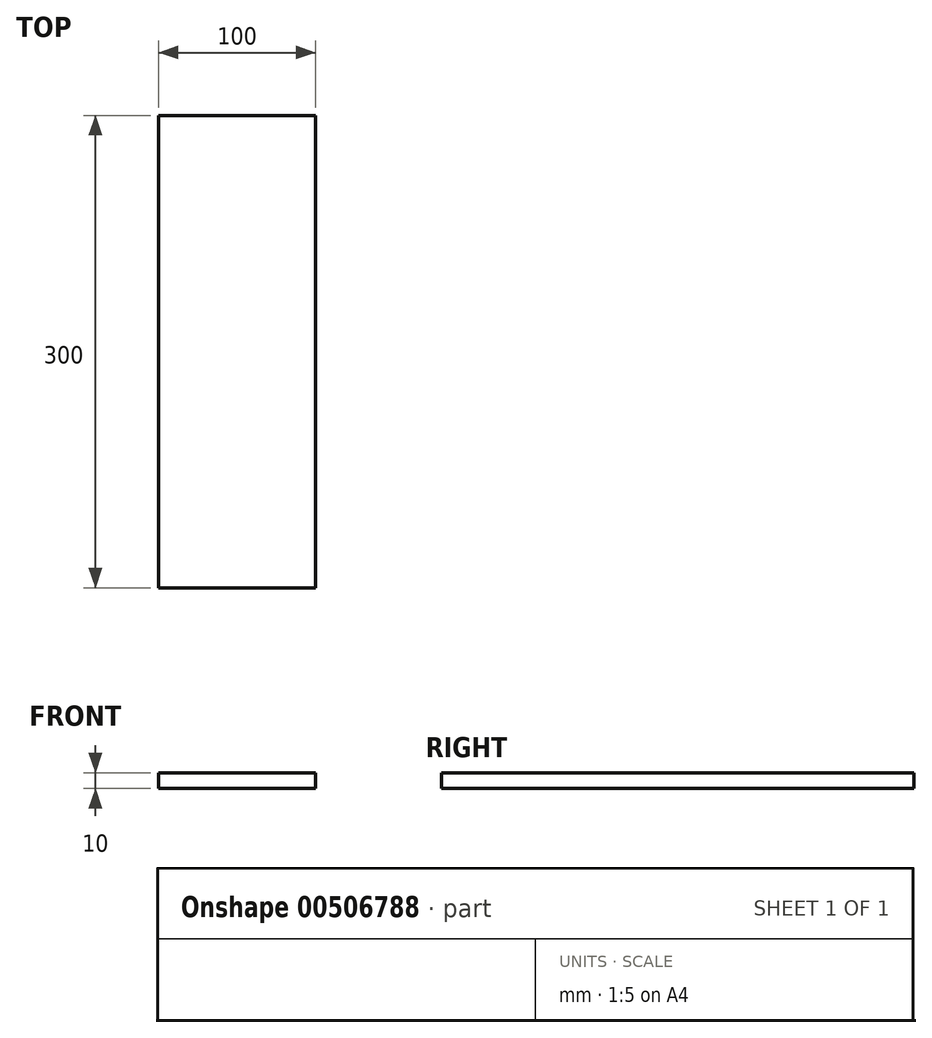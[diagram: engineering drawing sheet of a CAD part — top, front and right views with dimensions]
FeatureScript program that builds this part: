
annotation { "Feature Type Name" : "Feature", "Feature Type Description" : "" }
export const myFeature = defineFeature(function(context is Context, id is Id, definition is map)
    precondition{}
    {
        {
            var Q0;
            Q0=qCreatedBy(makeId("Front.planeOp"),FACE);
            var sketch = newSketch(context, id + "F0", { "sketchPlane" : qUnion([Q0])});
            skLineSegment(sketch, "E0.bottom", {"start": v(0, 0) * mm, "end": v(100, 0) * mm});
            skLineSegment(sketch, "E0.top", {"start": v(0, 10) * mm, "end": v(100, 10) * mm});
            skLineSegment(sketch, "E0.left", {"start": v(0, 0) * mm, "end": v(0, 10) * mm});
            skLineSegment(sketch, "E0.right", {"start": v(100, 0) * mm, "end": v(100, 10) * mm});
            skSolve(sketch);
        }
        {
            var Q0;
            Q0=makeQuery(id+"F0.imprint","IMPRINT",FACE,{"disambiguationData":[TD([[makeQuery(id+"F0.imprint","IMPRINT",EDGE,{"derivedFrom":sQuery(id+"F0.wireOp",EDGE,"E0.bottom")}),1.0]])]});
            extrude(context, id + "F1", {"entities" : qUnion([Q0]), "oppositeDirection" : true, "depth" : 300 * mm});
        }
    });
